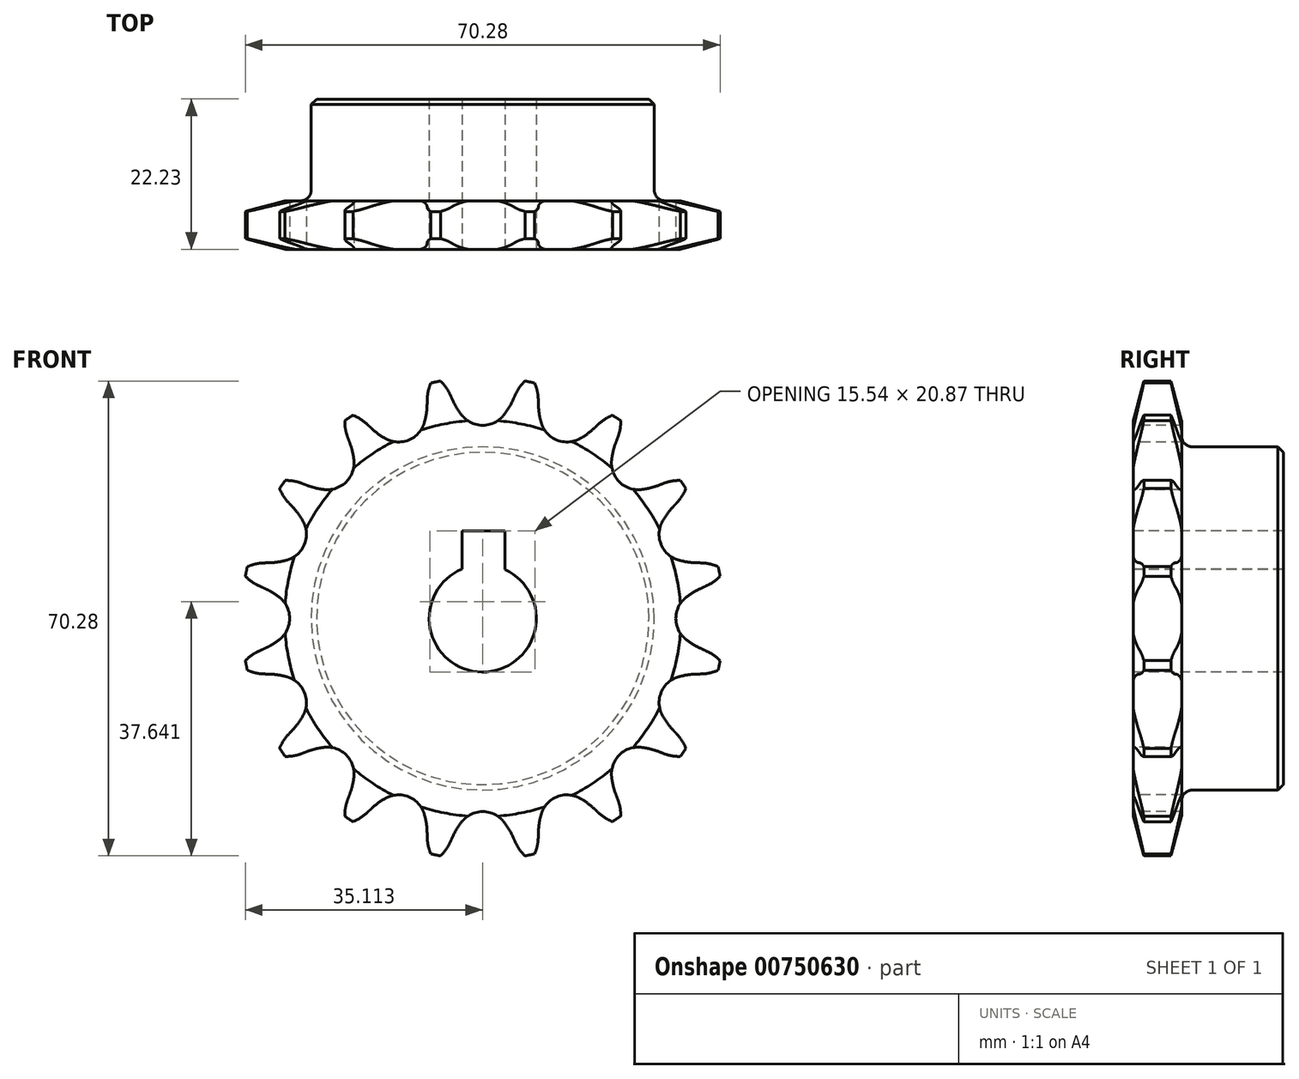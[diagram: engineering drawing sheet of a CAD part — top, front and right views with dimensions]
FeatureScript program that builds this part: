
annotation { "Feature Type Name" : "Feature", "Feature Type Description" : "" }
export const myFeature = defineFeature(function(context is Context, id is Id, definition is map)
    precondition{}
    {
        {
            var Q0;
            Q0=qCreatedBy(makeId("Right.planeOp"),FACE);
            var sketch = newSketch(context, id + "F0", { "sketchPlane" : qUnion([Q0])});
            skLineSegment(sketch, "E0", {"start": v(0, 0) * mm, "end": v(22.23, 0) * mm, "construction": true});
            skLineSegment(sketch, "E1.bottom", {"start": v(0, 7.94) * mm, "end": v(7.16, 7.94) * mm});
            skLineSegment(sketch, "E1.top", {"start": v(0, 35.69) * mm, "end": v(7.16, 35.69) * mm});
            skLineSegment(sketch, "E1.left", {"start": v(0, 7.94) * mm, "end": v(0, 35.69) * mm});
            skLineSegment(sketch, "E1.right", {"start": v(7.16, 7.94) * mm, "end": v(7.16, 35.69) * mm});
            skLineSegment(sketch, "E2.bottom", {"start": v(0, 7.94) * mm, "end": v(22.23, 7.94) * mm});
            skLineSegment(sketch, "E2.top", {"start": v(0, 25.4) * mm, "end": v(22.23, 25.4) * mm});
            skLineSegment(sketch, "E2.left", {"start": v(0, 7.94) * mm, "end": v(0, 25.4) * mm});
            skLineSegment(sketch, "E2.right", {"start": v(22.23, 7.94) * mm, "end": v(22.23, 25.4) * mm});
            skLineSegment(sketch, "E3.MirrorCS", {"start": v(0, -7.94) * mm, "end": v(7.16, -7.94) * mm});
            skLineSegment(sketch, "E4.MirrorCS", {"start": v(0, -25.4) * mm, "end": v(22.23, -25.4) * mm});
            skLineSegment(sketch, "E5.MirrorCS", {"start": v(0, -7.94) * mm, "end": v(22.23, -7.94) * mm});
            skLineSegment(sketch, "E6.MirrorCS", {"start": v(7.16, -7.94) * mm, "end": v(7.16, -35.69) * mm});
            skLineSegment(sketch, "E7.MirrorCS", {"start": v(0, -7.94) * mm, "end": v(0, -25.4) * mm});
            skLineSegment(sketch, "E8.MirrorCS", {"start": v(22.23, -7.94) * mm, "end": v(22.23, -25.4) * mm});
            skLineSegment(sketch, "E9.MirrorCS", {"start": v(0, -35.69) * mm, "end": v(7.16, -35.69) * mm});
            skLineSegment(sketch, "E10.MirrorCS", {"start": v(0, -7.94) * mm, "end": v(0, -35.69) * mm});
            skSolve(sketch);
        }
        {
            var Q0;
            {var subQ0=sQuery(id+"F0.wireOp",EDGE,"E1.top");Q0=makeQuery(id+"F0.imprint","IMPRINT",FACE,{"disambiguationData":[TD([[makeQuery(id+"F0.imprint","IMPRINT",EDGE,{"derivedFrom":subQ0}),-1.0]])]});}
            var Q1;
            {var subQ0=sQuery(id+"F0.wireOp",EDGE,"E1.bottom");Q1=makeQuery(id+"F0.imprint","IMPRINT",FACE,{"disambiguationData":[TD([[makeQuery(id+"F0.imprint","IMPRINT",EDGE,{"derivedFrom":subQ0}),1.0]])]});}
            var Q2;
            {var subQ0=sQuery(id+"F0.wireOp",EDGE,"E2.bottom");Q2=makeQuery(id+"F0.imprint","IMPRINT",FACE,{"disambiguationData":[TD([[makeQuery(id+"F0.imprint","IMPRINT",EDGE,{"derivedFrom":subQ0}),1.0]])]});}
            var Q3;
            Q3=sQuery(id+"F0.wireOp",EDGE,"E0");
            revolve(context, id + "F1", {"surfaceOperationType" : NewSurfaceOperationType.NEW, "entities" : qUnion([Q0, Q1, Q2]), "axis" : qUnion([Q3]), "revolveType" : RevolveType.FULL});
        }
        {
            var Q0;
            Q0=makeQuery(id+"F1.opRevolve","SWEPT_EDGE",EDGE,{"disambiguationData":[OSD([sQuery(id+"F0.wireOp",EDGE,"E1.right"),sQuery(id+"F0.wireOp",EDGE,"E2.top")])]});
            fillet(context, id + "F2", {"entities" : qUnion([Q0]), "radius" : 1.59 * mm, "tangentPropagation" : true, "allowEdgeOverflow" : false});
        }
        {
            var Q0;
            Q0=makeQuery(id+"F1.opRevolve","SWEPT_EDGE",EDGE,{"disambiguationData":[OSD([sQuery(id+"F0.wireOp",EDGE,"E2.top"),sQuery(id+"F0.wireOp",EDGE,"E2.right")])]});
            chamfer(context, id + "F3", {"entities" : qUnion([Q0]), "width" : 0.8 * mm, "tangentPropagation" : true});
        }
        {
            var Q0;
            Q0=makeQuery(id+"F1.opRevolve","SWEPT_EDGE",EDGE,{"disambiguationData":[OSD([sQuery(id+"F0.wireOp",EDGE,"E1.top"),sQuery(id+"F0.wireOp",EDGE,"E1.left")])]});
            var Q1;
            Q1=makeQuery(id+"F1.opRevolve","SWEPT_EDGE",EDGE,{"disambiguationData":[OSD([sQuery(id+"F0.wireOp",EDGE,"E1.top"),sQuery(id+"F0.wireOp",EDGE,"E1.right")])]});
            chamfer(context, id + "F4", {"entities" : qUnion([Q0, Q1]), "chamferType" : ChamferType.TWO_OFFSETS, "width1" : 6.35 * mm, "oppositeDirection" : false, "width2" : 1.57 * mm, "tangentPropagation" : true});
        }
        {
            var Q0;
            Q0=makeQuery(id+"F1.opRevolve","SWEPT_FACE",FACE,{"disambiguationData":[OSD([sQuery(id+"F0.wireOp",EDGE,"E1.left")])]});
            var sketch = newSketch(context, id + "F5", { "sketchPlane" : qUnion([Q0])});
            skCircle(sketch, "E11", {"center": v(0, 0) * mm, "radius": 32.55 * mm, "construction": true});
            skLineSegment(sketch, "E12", {"start": v(0, 0) * mm, "end": v(0, 32.55) * mm, "construction": true});
            skLineSegment(sketch, "E13", {"start": v(0, 32.55) * mm, "end": v(42.38, 32.55) * mm, "construction": true});
            skLineSegment(sketch, "E14", {"start": v(0, 32.55) * mm, "end": v(5, 36.56) * mm, "construction": true});
            skLineSegment(sketch, "E15", {"start": v(5, 36.56) * mm, "end": v(-4.46, 32.3) * mm, "construction": true});
            skLineSegment(sketch, "E16", {"start": v(-4.46, 32.3) * mm, "end": v(-4.82, 33.1) * mm});
            skLineSegment(sketch, "E17", {"start": v(0, 0) * mm, "end": v(-7.13, 35.85) * mm, "construction": true});
            skArc(sketch, "E18", {"start": v(-7.13, 35.85) * mm, "mid": v(-15.87, 26.15) * mm, "end": v(-4.82, 33.1) * mm, "construction": true});
            skArc(sketch, "E19", {"start": v(-4.82, 33.1) * mm, "mid": v(-5.78, 34.63) * mm, "end": v(-7.13, 35.85) * mm});
            skLineSegment(sketch, "E20", {"start": v(-4.82, 33.1) * mm, "end": v(-7.12, 38.2) * mm, "construction": true});
            skArc(sketch, "E21", {"start": v(-4.46, 32.3) * mm, "mid": v(-3.84, 31.14) * mm, "end": v(-3.1, 30.07) * mm});
            skArc(sketch, "E22", {"start": v(-3.1, 30.07) * mm, "mid": v(13.83, 41.97) * mm, "end": v(-4.46, 32.3) * mm, "construction": true});
            skLineSegment(sketch, "E23.MirrorCS", {"start": v(16.78, 7.56) * mm, "end": v(-7.6, 29.13) * mm, "construction": true});
            skArc(sketch, "E24.MirrorCS", {"start": v(4.46, 32.3) * mm, "mid": v(3.84, 31.14) * mm, "end": v(3.1, 30.07) * mm});
            skLineSegment(sketch, "E25.MirrorCS", {"start": v(4.46, 32.3) * mm, "end": v(4.82, 33.1) * mm});
            skArc(sketch, "E26.MirrorCS", {"start": v(4.82, 33.1) * mm, "mid": v(5.78, 34.63) * mm, "end": v(7.13, 35.85) * mm});
            skArc(sketch, "E27", {"start": v(3.1, 30.07) * mm, "mid": v(0, 36.51) * mm, "end": v(-3.1, 30.07) * mm, "construction": true});
            skArc(sketch, "E28", {"start": v(-3.1, 30.07) * mm, "mid": v(0, 28.59) * mm, "end": v(3.1, 30.07) * mm});
            skLineSegment(sketch, "E29", {"start": v(3.1, 30.07) * mm, "end": v(3.1, 30.07) * mm});
            skArc(sketch, "E30.1.0", {"start": v(-17.12, 28.74) * mm, "mid": v(-18.6, 29.79) * mm, "end": v(-20.3, 30.4) * mm});
            skLineSegment(sketch, "E30.1.1", {"start": v(-16.48, 28.14) * mm, "end": v(-17.12, 28.74) * mm});
            skArc(sketch, "E30.1.2", {"start": v(-16.48, 28.14) * mm, "mid": v(-15.47, 27.3) * mm, "end": v(-14.36, 26.6) * mm});
            skArc(sketch, "E30.1.3", {"start": v(-14.36, 26.6) * mm, "mid": v(-10.94, 26.41) * mm, "end": v(-8.65, 28.96) * mm});
            skArc(sketch, "E30.1.4", {"start": v(-8.24, 31.55) * mm, "mid": v(-8.37, 30.24) * mm, "end": v(-8.65, 28.96) * mm});
            skLineSegment(sketch, "E30.1.5", {"start": v(-8.24, 31.55) * mm, "end": v(-8.22, 32.42) * mm});
            skArc(sketch, "E30.1.6", {"start": v(-8.22, 32.42) * mm, "mid": v(-7.91, 34.21) * mm, "end": v(-7.13, 35.85) * mm});
            skArc(sketch, "E30.2.0", {"start": v(-26.8, 20) * mm, "mid": v(-28.58, 20.4) * mm, "end": v(-30.4, 20.3) * mm});
            skLineSegment(sketch, "E30.2.1", {"start": v(-26, 19.69) * mm, "end": v(-26.8, 20) * mm});
            skArc(sketch, "E30.2.2", {"start": v(-26, 19.69) * mm, "mid": v(-24.74, 19.3) * mm, "end": v(-23.45, 19.08) * mm});
            skArc(sketch, "E30.2.3", {"start": v(-23.45, 19.08) * mm, "mid": v(-20.21, 20.21) * mm, "end": v(-19.08, 23.45) * mm});
            skArc(sketch, "E30.2.4", {"start": v(-19.69, 26) * mm, "mid": v(-19.3, 24.74) * mm, "end": v(-19.08, 23.45) * mm});
            skLineSegment(sketch, "E30.2.5", {"start": v(-19.69, 26) * mm, "end": v(-20, 26.8) * mm});
            skArc(sketch, "E30.2.6", {"start": v(-20, 26.8) * mm, "mid": v(-20.4, 28.58) * mm, "end": v(-20.3, 30.4) * mm});
            skArc(sketch, "E30.3.0", {"start": v(-32.42, 8.22) * mm, "mid": v(-34.21, 7.91) * mm, "end": v(-35.85, 7.13) * mm});
            skLineSegment(sketch, "E30.3.1", {"start": v(-31.55, 8.24) * mm, "end": v(-32.42, 8.22) * mm});
            skArc(sketch, "E30.3.2", {"start": v(-31.55, 8.24) * mm, "mid": v(-30.24, 8.37) * mm, "end": v(-28.96, 8.65) * mm});
            skArc(sketch, "E30.3.3", {"start": v(-28.96, 8.65) * mm, "mid": v(-26.41, 10.94) * mm, "end": v(-26.6, 14.36) * mm});
            skArc(sketch, "E30.3.4", {"start": v(-28.14, 16.48) * mm, "mid": v(-27.3, 15.47) * mm, "end": v(-26.6, 14.36) * mm});
            skLineSegment(sketch, "E30.3.5", {"start": v(-28.14, 16.48) * mm, "end": v(-28.74, 17.12) * mm});
            skArc(sketch, "E30.3.6", {"start": v(-28.74, 17.12) * mm, "mid": v(-29.79, 18.6) * mm, "end": v(-30.4, 20.3) * mm});
            skArc(sketch, "E30.4.0", {"start": v(-33.1, -4.82) * mm, "mid": v(-34.63, -5.78) * mm, "end": v(-35.85, -7.13) * mm});
            skLineSegment(sketch, "E30.4.1", {"start": v(-32.3, -4.46) * mm, "end": v(-33.1, -4.82) * mm});
            skArc(sketch, "E30.4.2", {"start": v(-32.3, -4.46) * mm, "mid": v(-31.14, -3.84) * mm, "end": v(-30.07, -3.1) * mm});
            skArc(sketch, "E30.4.3", {"start": v(-30.07, -3.1) * mm, "mid": v(-28.59, 0) * mm, "end": v(-30.07, 3.1) * mm});
            skArc(sketch, "E30.4.4", {"start": v(-32.3, 4.46) * mm, "mid": v(-31.14, 3.84) * mm, "end": v(-30.07, 3.1) * mm});
            skLineSegment(sketch, "E30.4.5", {"start": v(-32.3, 4.46) * mm, "end": v(-33.1, 4.82) * mm});
            skArc(sketch, "E30.4.6", {"start": v(-33.1, 4.82) * mm, "mid": v(-34.63, 5.78) * mm, "end": v(-35.85, 7.13) * mm});
            skArc(sketch, "E30.5.0", {"start": v(-28.74, -17.12) * mm, "mid": v(-29.79, -18.6) * mm, "end": v(-30.4, -20.3) * mm});
            skLineSegment(sketch, "E30.5.1", {"start": v(-28.14, -16.48) * mm, "end": v(-28.74, -17.12) * mm});
            skArc(sketch, "E30.5.2", {"start": v(-28.14, -16.48) * mm, "mid": v(-27.3, -15.47) * mm, "end": v(-26.6, -14.36) * mm});
            skArc(sketch, "E30.5.3", {"start": v(-26.6, -14.36) * mm, "mid": v(-26.41, -10.94) * mm, "end": v(-28.96, -8.65) * mm});
            skArc(sketch, "E30.5.4", {"start": v(-31.55, -8.24) * mm, "mid": v(-30.24, -8.37) * mm, "end": v(-28.96, -8.65) * mm});
            skLineSegment(sketch, "E30.5.5", {"start": v(-31.55, -8.24) * mm, "end": v(-32.42, -8.22) * mm});
            skArc(sketch, "E30.5.6", {"start": v(-32.42, -8.22) * mm, "mid": v(-34.21, -7.91) * mm, "end": v(-35.85, -7.13) * mm});
            skArc(sketch, "E30.6.0", {"start": v(-20, -26.8) * mm, "mid": v(-20.4, -28.58) * mm, "end": v(-20.3, -30.4) * mm});
            skLineSegment(sketch, "E30.6.1", {"start": v(-19.69, -26) * mm, "end": v(-20, -26.8) * mm});
            skArc(sketch, "E30.6.2", {"start": v(-19.69, -26) * mm, "mid": v(-19.3, -24.74) * mm, "end": v(-19.08, -23.45) * mm});
            skArc(sketch, "E30.6.3", {"start": v(-19.08, -23.45) * mm, "mid": v(-20.21, -20.21) * mm, "end": v(-23.45, -19.08) * mm});
            skArc(sketch, "E30.6.4", {"start": v(-26, -19.69) * mm, "mid": v(-24.74, -19.3) * mm, "end": v(-23.45, -19.08) * mm});
            skLineSegment(sketch, "E30.6.5", {"start": v(-26, -19.69) * mm, "end": v(-26.8, -20) * mm});
            skArc(sketch, "E30.6.6", {"start": v(-26.8, -20) * mm, "mid": v(-28.58, -20.4) * mm, "end": v(-30.4, -20.3) * mm});
            skArc(sketch, "E30.7.0", {"start": v(-8.22, -32.42) * mm, "mid": v(-7.91, -34.21) * mm, "end": v(-7.13, -35.85) * mm});
            skLineSegment(sketch, "E30.7.1", {"start": v(-8.24, -31.55) * mm, "end": v(-8.22, -32.42) * mm});
            skArc(sketch, "E30.7.2", {"start": v(-8.24, -31.55) * mm, "mid": v(-8.37, -30.24) * mm, "end": v(-8.65, -28.96) * mm});
            skArc(sketch, "E30.7.3", {"start": v(-8.65, -28.96) * mm, "mid": v(-10.94, -26.41) * mm, "end": v(-14.36, -26.6) * mm});
            skArc(sketch, "E30.7.4", {"start": v(-16.48, -28.14) * mm, "mid": v(-15.47, -27.3) * mm, "end": v(-14.36, -26.6) * mm});
            skLineSegment(sketch, "E30.7.5", {"start": v(-16.48, -28.14) * mm, "end": v(-17.12, -28.74) * mm});
            skArc(sketch, "E30.7.6", {"start": v(-17.12, -28.74) * mm, "mid": v(-18.6, -29.79) * mm, "end": v(-20.3, -30.4) * mm});
            skArc(sketch, "E30.8.0", {"start": v(4.82, -33.1) * mm, "mid": v(5.78, -34.63) * mm, "end": v(7.13, -35.85) * mm});
            skLineSegment(sketch, "E30.8.1", {"start": v(4.46, -32.3) * mm, "end": v(4.82, -33.1) * mm});
            skArc(sketch, "E30.8.2", {"start": v(4.46, -32.3) * mm, "mid": v(3.84, -31.14) * mm, "end": v(3.1, -30.07) * mm});
            skArc(sketch, "E30.8.3", {"start": v(3.1, -30.07) * mm, "mid": v(0, -28.59) * mm, "end": v(-3.1, -30.07) * mm});
            skArc(sketch, "E30.8.4", {"start": v(-4.46, -32.3) * mm, "mid": v(-3.84, -31.14) * mm, "end": v(-3.1, -30.07) * mm});
            skLineSegment(sketch, "E30.8.5", {"start": v(-4.46, -32.3) * mm, "end": v(-4.82, -33.1) * mm});
            skArc(sketch, "E30.8.6", {"start": v(-4.82, -33.1) * mm, "mid": v(-5.78, -34.63) * mm, "end": v(-7.13, -35.85) * mm});
            skArc(sketch, "E30.9.0", {"start": v(17.12, -28.74) * mm, "mid": v(18.6, -29.79) * mm, "end": v(20.3, -30.4) * mm});
            skLineSegment(sketch, "E30.9.1", {"start": v(16.48, -28.14) * mm, "end": v(17.12, -28.74) * mm});
            skArc(sketch, "E30.9.2", {"start": v(16.48, -28.14) * mm, "mid": v(15.47, -27.3) * mm, "end": v(14.36, -26.6) * mm});
            skArc(sketch, "E30.9.3", {"start": v(14.36, -26.6) * mm, "mid": v(10.94, -26.41) * mm, "end": v(8.65, -28.96) * mm});
            skArc(sketch, "E30.9.4", {"start": v(8.24, -31.55) * mm, "mid": v(8.37, -30.24) * mm, "end": v(8.65, -28.96) * mm});
            skLineSegment(sketch, "E30.9.5", {"start": v(8.24, -31.55) * mm, "end": v(8.22, -32.42) * mm});
            skArc(sketch, "E30.9.6", {"start": v(8.22, -32.42) * mm, "mid": v(7.91, -34.21) * mm, "end": v(7.13, -35.85) * mm});
            skArc(sketch, "E30.10.0", {"start": v(26.8, -20) * mm, "mid": v(28.58, -20.4) * mm, "end": v(30.4, -20.3) * mm});
            skLineSegment(sketch, "E30.10.1", {"start": v(26, -19.69) * mm, "end": v(26.8, -20) * mm});
            skArc(sketch, "E30.10.2", {"start": v(26, -19.69) * mm, "mid": v(24.74, -19.3) * mm, "end": v(23.45, -19.08) * mm});
            skArc(sketch, "E30.10.3", {"start": v(23.45, -19.08) * mm, "mid": v(20.21, -20.21) * mm, "end": v(19.08, -23.45) * mm});
            skArc(sketch, "E30.10.4", {"start": v(19.69, -26) * mm, "mid": v(19.3, -24.74) * mm, "end": v(19.08, -23.45) * mm});
            skLineSegment(sketch, "E30.10.5", {"start": v(19.69, -26) * mm, "end": v(20, -26.8) * mm});
            skArc(sketch, "E30.10.6", {"start": v(20, -26.8) * mm, "mid": v(20.4, -28.58) * mm, "end": v(20.3, -30.4) * mm});
            skArc(sketch, "E30.11.0", {"start": v(32.42, -8.22) * mm, "mid": v(34.21, -7.91) * mm, "end": v(35.85, -7.13) * mm});
            skLineSegment(sketch, "E30.11.1", {"start": v(31.55, -8.24) * mm, "end": v(32.42, -8.22) * mm});
            skArc(sketch, "E30.11.2", {"start": v(31.55, -8.24) * mm, "mid": v(30.24, -8.37) * mm, "end": v(28.96, -8.65) * mm});
            skArc(sketch, "E30.11.3", {"start": v(28.96, -8.65) * mm, "mid": v(26.41, -10.94) * mm, "end": v(26.6, -14.36) * mm});
            skArc(sketch, "E30.11.4", {"start": v(28.14, -16.48) * mm, "mid": v(27.3, -15.47) * mm, "end": v(26.6, -14.36) * mm});
            skLineSegment(sketch, "E30.11.5", {"start": v(28.14, -16.48) * mm, "end": v(28.74, -17.12) * mm});
            skArc(sketch, "E30.11.6", {"start": v(28.74, -17.12) * mm, "mid": v(29.79, -18.6) * mm, "end": v(30.4, -20.3) * mm});
            skArc(sketch, "E30.12.0", {"start": v(33.1, 4.82) * mm, "mid": v(34.63, 5.78) * mm, "end": v(35.85, 7.13) * mm});
            skLineSegment(sketch, "E30.12.1", {"start": v(32.3, 4.46) * mm, "end": v(33.1, 4.82) * mm});
            skArc(sketch, "E30.12.2", {"start": v(32.3, 4.46) * mm, "mid": v(31.14, 3.84) * mm, "end": v(30.07, 3.1) * mm});
            skArc(sketch, "E30.12.3", {"start": v(30.07, 3.1) * mm, "mid": v(28.59, 0) * mm, "end": v(30.07, -3.1) * mm});
            skArc(sketch, "E30.12.4", {"start": v(32.3, -4.46) * mm, "mid": v(31.14, -3.84) * mm, "end": v(30.07, -3.1) * mm});
            skLineSegment(sketch, "E30.12.5", {"start": v(32.3, -4.46) * mm, "end": v(33.1, -4.82) * mm});
            skArc(sketch, "E30.12.6", {"start": v(33.1, -4.82) * mm, "mid": v(34.63, -5.78) * mm, "end": v(35.85, -7.13) * mm});
            skArc(sketch, "E30.13.0", {"start": v(28.74, 17.12) * mm, "mid": v(29.79, 18.6) * mm, "end": v(30.4, 20.3) * mm});
            skLineSegment(sketch, "E30.13.1", {"start": v(28.14, 16.48) * mm, "end": v(28.74, 17.12) * mm});
            skArc(sketch, "E30.13.2", {"start": v(28.14, 16.48) * mm, "mid": v(27.3, 15.47) * mm, "end": v(26.6, 14.36) * mm});
            skArc(sketch, "E30.13.3", {"start": v(26.6, 14.36) * mm, "mid": v(26.41, 10.94) * mm, "end": v(28.96, 8.65) * mm});
            skArc(sketch, "E30.13.4", {"start": v(31.55, 8.24) * mm, "mid": v(30.24, 8.37) * mm, "end": v(28.96, 8.65) * mm});
            skLineSegment(sketch, "E30.13.5", {"start": v(31.55, 8.24) * mm, "end": v(32.42, 8.22) * mm});
            skArc(sketch, "E30.13.6", {"start": v(32.42, 8.22) * mm, "mid": v(34.21, 7.91) * mm, "end": v(35.85, 7.13) * mm});
            skArc(sketch, "E30.14.0", {"start": v(20, 26.8) * mm, "mid": v(20.4, 28.58) * mm, "end": v(20.3, 30.4) * mm});
            skLineSegment(sketch, "E30.14.1", {"start": v(19.69, 26) * mm, "end": v(20, 26.8) * mm});
            skArc(sketch, "E30.14.2", {"start": v(19.69, 26) * mm, "mid": v(19.3, 24.74) * mm, "end": v(19.08, 23.45) * mm});
            skArc(sketch, "E30.14.3", {"start": v(19.08, 23.45) * mm, "mid": v(20.21, 20.21) * mm, "end": v(23.45, 19.08) * mm});
            skArc(sketch, "E30.14.4", {"start": v(26, 19.69) * mm, "mid": v(24.74, 19.3) * mm, "end": v(23.45, 19.08) * mm});
            skLineSegment(sketch, "E30.14.5", {"start": v(26, 19.69) * mm, "end": v(26.8, 20) * mm});
            skArc(sketch, "E30.14.6", {"start": v(26.8, 20) * mm, "mid": v(28.58, 20.4) * mm, "end": v(30.4, 20.3) * mm});
            skArc(sketch, "E30.15.0", {"start": v(8.22, 32.42) * mm, "mid": v(7.91, 34.21) * mm, "end": v(7.13, 35.85) * mm});
            skLineSegment(sketch, "E30.15.1", {"start": v(8.24, 31.55) * mm, "end": v(8.22, 32.42) * mm});
            skArc(sketch, "E30.15.2", {"start": v(8.24, 31.55) * mm, "mid": v(8.37, 30.24) * mm, "end": v(8.65, 28.96) * mm});
            skArc(sketch, "E30.15.3", {"start": v(8.65, 28.96) * mm, "mid": v(10.94, 26.41) * mm, "end": v(14.36, 26.6) * mm});
            skArc(sketch, "E30.15.4", {"start": v(16.48, 28.14) * mm, "mid": v(15.47, 27.3) * mm, "end": v(14.36, 26.6) * mm});
            skLineSegment(sketch, "E30.15.5", {"start": v(16.48, 28.14) * mm, "end": v(17.12, 28.74) * mm});
            skArc(sketch, "E30.15.6", {"start": v(17.12, 28.74) * mm, "mid": v(18.6, 29.79) * mm, "end": v(20.3, 30.4) * mm});
            skSolve(sketch);
        }
        {
            var Q0;
            Q0 = qSketchRegion(id + "F5", true);
            extrude(context, id + "F6", {"entities" : qUnion([Q0]), "operationType" : NewBodyOperationType.INTERSECT, "endBound" : BoundingType.THROUGH_ALL, "oppositeDirection" : true, "depth" : 25.4 * mm, "offsetDistance" : 25.4 * mm});
        }
        {
            var Q0;
            Q0=makeQuery(id+"F1.opRevolve","SWEPT_FACE",FACE,{"disambiguationData":[OSD([sQuery(id+"F0.wireOp",EDGE,"E1.left")])]});
            var sketch = newSketch(context, id + "F7", { "sketchPlane" : qUnion([Q0])});
            skLineSegment(sketch, "E31.bottom", {"start": v(-3.05, 12.94) * mm, "end": v(3.3, 12.94) * mm});
            skLineSegment(sketch, "E31.top", {"start": v(-3.05, 6.59) * mm, "end": v(3.3, 6.59) * mm});
            skLineSegment(sketch, "E31.left", {"start": v(-3.05, 12.94) * mm, "end": v(-3.05, 6.59) * mm});
            skLineSegment(sketch, "E31.right", {"start": v(3.3, 12.94) * mm, "end": v(3.3, 6.59) * mm});
            skLineSegment(sketch, "E32", {"start": v(0, 0) * mm, "end": v(0, 15.09) * mm, "construction": true});
            skSolve(sketch);
        }
        {
            var Q0;
            Q0 = qSketchRegion(id + "F7", true);
            extrude(context, id + "F8", {"entities" : qUnion([Q0]), "operationType" : NewBodyOperationType.REMOVE, "endBound" : BoundingType.THROUGH_ALL, "oppositeDirection" : true, "depth" : 25.4 * mm, "offsetDistance" : 25.4 * mm});
        }
    });
